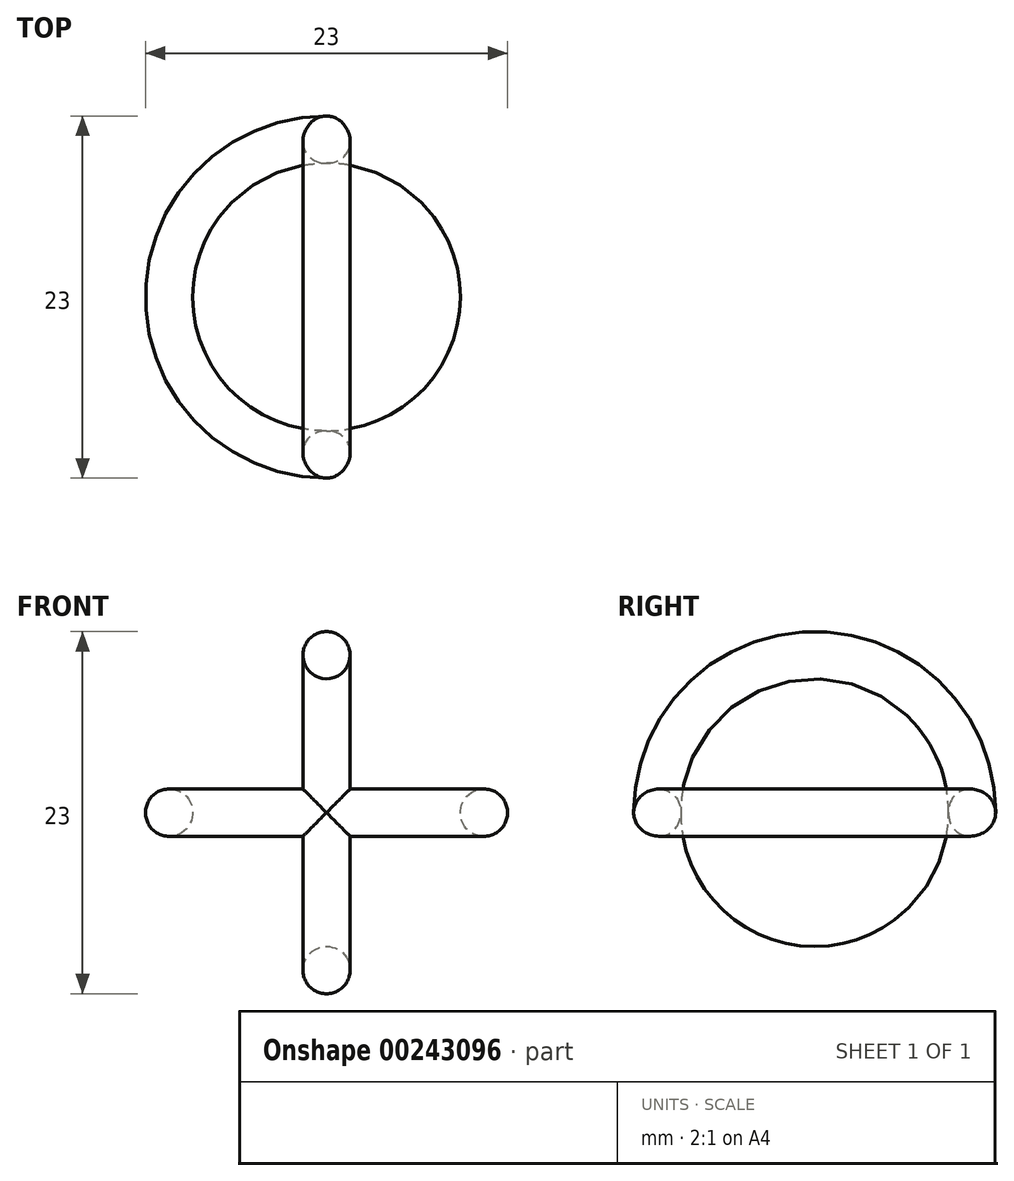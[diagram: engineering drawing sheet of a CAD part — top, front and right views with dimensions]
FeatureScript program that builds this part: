
annotation { "Feature Type Name" : "Feature", "Feature Type Description" : "" }
export const myFeature = defineFeature(function(context is Context, id is Id, definition is map)
    precondition{}
    {
        {
            var Q0;
            Q0=qCreatedBy(makeId("Front.planeOp"),FACE);
            var sketch = newSketch(context, id + "F0", { "sketchPlane" : qUnion([Q0])});
            skLineSegment(sketch, "E0", {"start": v(0, 0) * mm, "end": v(10, 0) * mm, "construction": true});
            skLineSegment(sketch, "E1", {"start": v(0, 0) * mm, "end": v(0, 10) * mm, "construction": true});
            skCircle(sketch, "E2", {"center": v(10, 0) * mm, "radius": 1.5 * mm});
            skCircle(sketch, "E3", {"center": v(0, 10) * mm, "radius": 1.5 * mm});
            skSolve(sketch);
        }
        {
            var Q0;
            Q0=makeQuery(id+"F0.imprint","IMPRINT",FACE,{"disambiguationData":[TD([[makeQuery(id+"F0.imprint","IMPRINT",EDGE,{"derivedFrom":sQuery(id+"F0.wireOp",EDGE,"E3")}),1.0]])]});
            var Q1;
            Q1=sQuery(id+"F0.wireOp",EDGE,"E0");
            revolve(context, id + "F1", {"entities" : qUnion([Q0]), "axis" : qUnion([Q1]), "revolveType" : RevolveType.FULL});
        }
        {
            var Q0;
            Q0=makeQuery(id+"F0.imprint","IMPRINT",FACE,{"disambiguationData":[TD([[makeQuery(id+"F0.imprint","IMPRINT",EDGE,{"derivedFrom":sQuery(id+"F0.wireOp",EDGE,"E2")}),1.0]])]});
            var Q1;
            Q1=sQuery(id+"F0.wireOp",EDGE,"E1");
            revolve(context, id + "F2", {"operationType" : NewBodyOperationType.ADD, "entities" : qUnion([Q0]), "axis" : qUnion([Q1]), "revolveType" : RevolveType.FULL});
        }
    });
